# Revit family: Скамейка без спинки «Астана»
name_source: partatom
category: Антураж
revit_build: Autodesk Revit 2017 (Build: 20170118_1100(x64)
units: mm (PartAtom-declared; Revit-internal decimal feet)

## family parameters
Всегда вертикально = Да
Источник визуального образа = Геометрия семейства
На основе рабочей плоскости = Нет
Общий = Нет
При загрузке вырезать с полостями = Нет
Точка расчета площади = Нет

## types (2) — shared parameters
ADSK_Код изделия = 11209
ADSK_Материал опоры = FS_Металл_Оцинкованный_Хром
ADSK_Наименование = Скамейка без спинки «Астана»
ADSK_Размер_Высота = 400 мм
ADSK_Размер_Длина = 1800 мм
ADSK_Размер_Ширина = 800 мм
URL = https://hobbyka.ru
Изготовитель = ООО "Хоббика"
zero-valued in all types: Высота

## per-type parameters (varying)
| type | ADSK_Материал доски | Стоимость |
| Скамейка без спинки «Астана»_Сосна | FS_Древесина_Сосна тонированная_Груша | 66905 $ |
| Скамейка без спинки «Астана»_Лиственница | FS_Древесина_Лиственница тонированная_Груша | 92458 $ |
